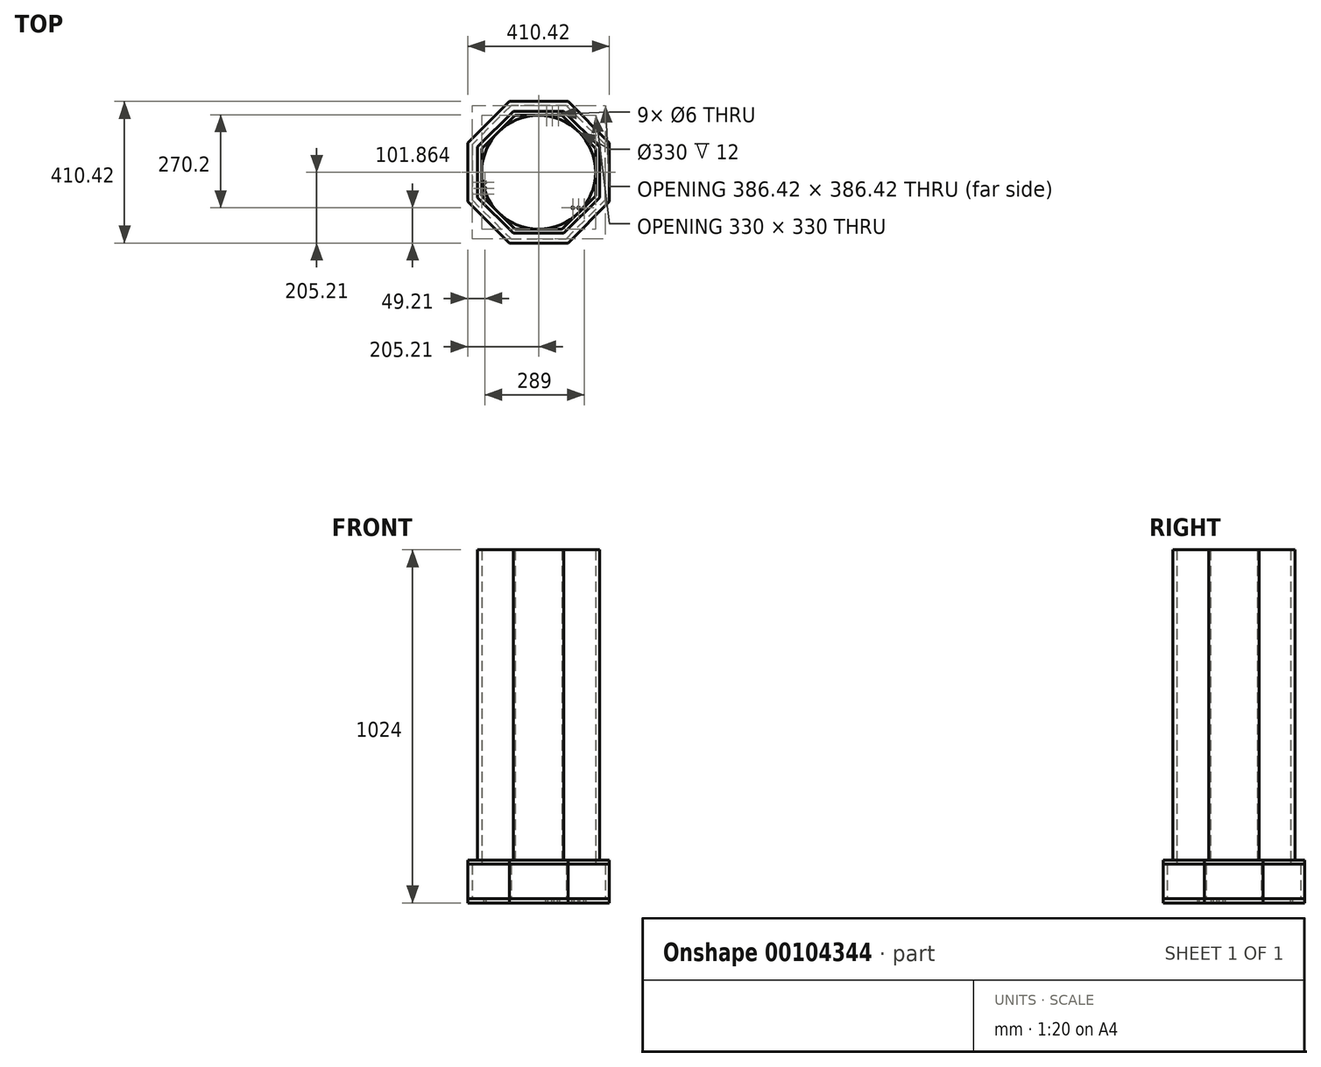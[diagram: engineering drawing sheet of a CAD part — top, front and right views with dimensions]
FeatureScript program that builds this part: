
annotation { "Feature Type Name" : "Feature", "Feature Type Description" : "" }
export const myFeature = defineFeature(function(context is Context, id is Id, definition is map)
    precondition{}
    {
        {
            var Q0;
            Q0=qCreatedBy(makeId("Top.planeOp"),FACE);
            var sketch = newSketch(context, id + "F0", { "sketchPlane" : qUnion([Q0])});
            skLineSegment(sketch, "E0.bottom", {"start": v(-85, 205.2) * mm, "end": v(85, 205.2) * mm});
            skLineSegment(sketch, "E0.top", {"start": v(-85, -205.2) * mm, "end": v(85, -205.2) * mm});
            skLineSegment(sketch, "E0.left", {"start": v(-205.2, 85) * mm, "end": v(-205.2, -85) * mm});
            skLineSegment(sketch, "E0.right", {"start": v(205.2, 85) * mm, "end": v(205.2, -85) * mm});
            skLineSegment(sketch, "E1", {"start": v(0, 127.02) * mm, "end": v(0, -63.5) * mm, "construction": true});
            skLineSegment(sketch, "E2", {"start": v(-110, -63.5) * mm, "end": v(55, 31.75) * mm, "construction": true});
            skLineSegment(sketch, "E3", {"start": v(110, -63.5) * mm, "end": v(-110, -63.5) * mm, "construction": true});
            skLineSegment(sketch, "E4", {"start": v(-110, -63.5) * mm, "end": v(-156, -63.5) * mm, "construction": true});
            skLineSegment(sketch, "E5", {"start": v(-110, -63.5) * mm, "end": v(0, 127.02) * mm, "construction": true});
            skLineSegment(sketch, "E6", {"start": v(0, 127.02) * mm, "end": v(110, -63.5) * mm, "construction": true});
            skLineSegment(sketch, "E7", {"start": v(-156, -63.5) * mm, "end": v(-156, -29.5) * mm, "construction": true});
            skCircle(sketch, "E8", {"center": v(-156, -29.5) * mm, "radius": 3 * mm});
            skCircle(sketch, "E9", {"center": v(-156, -46.5) * mm, "radius": 3 * mm});
            skCircle(sketch, "E10", {"center": v(-156, -63.5) * mm, "radius": 3 * mm});
            skPoint(sketch, "E11.center", {"position": v(0, 0) * mm});
            skLineSegment(sketch, "E12", {"start": v(0, 127.02) * mm, "end": v(23, 166.85) * mm, "construction": true});
            skLineSegment(sketch, "E13", {"start": v(110, -63.5) * mm, "end": v(133, -103.35) * mm, "construction": true});
            skLineSegment(sketch, "E14", {"start": v(23, 166.85) * mm, "end": v(57, 166.85) * mm, "construction": true});
            skLineSegment(sketch, "E15", {"start": v(99, -103.35) * mm, "end": v(133, -103.35) * mm, "construction": true});
            skCircle(sketch, "E16", {"center": v(23, 166.85) * mm, "radius": 3 * mm});
            skCircle(sketch, "E17", {"center": v(40, 166.85) * mm, "radius": 3 * mm});
            skCircle(sketch, "E18", {"center": v(57, 166.85) * mm, "radius": 3 * mm});
            skCircle(sketch, "E19", {"center": v(133, -103.35) * mm, "radius": 3 * mm});
            skCircle(sketch, "E20", {"center": v(116, -103.35) * mm, "radius": 3 * mm});
            skCircle(sketch, "E21", {"center": v(99, -103.35) * mm, "radius": 3 * mm});
            skLineSegment(sketch, "E22", {"start": v(-205.2, 85) * mm, "end": v(-85, 205.2) * mm});
            skCircle(sketch, "E23", {"center": v(0, 0) * mm, "radius": 205.2 * mm, "construction": true});
            skLineSegment(sketch, "E24", {"start": v(-205.2, -85) * mm, "end": v(-85, -205.2) * mm});
            skLineSegment(sketch, "E25", {"start": v(85, -205.2) * mm, "end": v(205.2, -85) * mm});
            skLineSegment(sketch, "E26", {"start": v(205.2, 85) * mm, "end": v(85, 205.2) * mm});
            skSolve(sketch);
        }
        {
            var Q0;
            Q0 = qSketchRegion(id + "F0", true);
            extrude(context, id + "F1", {"entities" : qUnion([Q0]), "depth" : 12 * mm});
        }
        {
            var Q0;
            Q0=makeQuery(id+"F1.opExtrude","CAP_FACE",FACE,{"disambiguationData":[OSD([sQuery(id+"F0.wireOp",EDGE,"E0.bottom"),sQuery(id+"F0.wireOp",EDGE,"E0.top"),sQuery(id+"F0.wireOp",EDGE,"E0.left"),sQuery(id+"F0.wireOp",EDGE,"E0.right"),sQuery(id+"F0.wireOp",EDGE,"E8"),sQuery(id+"F0.wireOp",EDGE,"E9"),sQuery(id+"F0.wireOp",EDGE,"E10"),sQuery(id+"F0.wireOp",EDGE,"E16"),sQuery(id+"F0.wireOp",EDGE,"E17"),sQuery(id+"F0.wireOp",EDGE,"E18"),sQuery(id+"F0.wireOp",EDGE,"E19"),sQuery(id+"F0.wireOp",EDGE,"E20"),sQuery(id+"F0.wireOp",EDGE,"E21"),sQuery(id+"F0.wireOp",EDGE,"E22"),sQuery(id+"F0.wireOp",EDGE,"E24"),sQuery(id+"F0.wireOp",EDGE,"E25"),sQuery(id+"F0.wireOp",EDGE,"E26")])],"isStart":false});
            var sketch = newSketch(context, id + "F2", { "sketchPlane" : qUnion([Q0])});
            skLineSegment(sketch, "E27", {"start": v(-80.03, -193.2) * mm, "end": v(80.03, -193.2) * mm});
            skLineSegment(sketch, "E28", {"start": v(80.03, -193.2) * mm, "end": v(193.2, -80.03) * mm});
            skLineSegment(sketch, "E29", {"start": v(193.2, -80.03) * mm, "end": v(193.2, 80.03) * mm});
            skLineSegment(sketch, "E30", {"start": v(193.2, 80.03) * mm, "end": v(80.03, 193.2) * mm});
            skLineSegment(sketch, "E31", {"start": v(80.03, 193.2) * mm, "end": v(-80.03, 193.2) * mm});
            skLineSegment(sketch, "E32", {"start": v(-80.03, 193.2) * mm, "end": v(-193.2, 80.03) * mm});
            skLineSegment(sketch, "E33", {"start": v(-193.2, 80.03) * mm, "end": v(-193.2, -80.03) * mm});
            skLineSegment(sketch, "E34", {"start": v(-193.2, -80.03) * mm, "end": v(-80.03, -193.2) * mm});
            skLineSegment(sketch, "E35", {"start": v(-205.2, 85) * mm, "end": v(-205.2, -85) * mm});
            skLineSegment(sketch, "E36", {"start": v(-205.2, -85) * mm, "end": v(-85, -205.2) * mm});
            skLineSegment(sketch, "E37", {"start": v(-85, -205.2) * mm, "end": v(85, -205.2) * mm});
            skLineSegment(sketch, "E38", {"start": v(85, -205.2) * mm, "end": v(205.2, -85) * mm});
            skLineSegment(sketch, "E39", {"start": v(205.2, -85) * mm, "end": v(205.2, 85) * mm});
            skLineSegment(sketch, "E40", {"start": v(205.2, 85) * mm, "end": v(85, 205.2) * mm});
            skLineSegment(sketch, "E41", {"start": v(85, 205.2) * mm, "end": v(-85, 205.2) * mm});
            skLineSegment(sketch, "E42", {"start": v(-85, 205.2) * mm, "end": v(-205.2, 85) * mm});
            skLineSegment(sketch, "E43", {"start": v(-193.2, 80.03) * mm, "end": v(-205.2, 80.03) * mm, "construction": true});
            skLineSegment(sketch, "E44", {"start": v(-80.03, 193.2) * mm, "end": v(-88.51, 201.7) * mm, "construction": true});
            skLineSegment(sketch, "E45", {"start": v(80.03, 193.2) * mm, "end": v(80.03, 205.2) * mm, "construction": true});
            skLineSegment(sketch, "E46", {"start": v(193.2, 80.03) * mm, "end": v(201.7, 88.51) * mm, "construction": true});
            skLineSegment(sketch, "E47", {"start": v(193.2, -80.03) * mm, "end": v(205.2, -80.03) * mm, "construction": true});
            skLineSegment(sketch, "E48", {"start": v(80.03, -193.2) * mm, "end": v(88.51, -201.7) * mm, "construction": true});
            skLineSegment(sketch, "E49", {"start": v(-80.03, -193.2) * mm, "end": v(-80.03, -205.2) * mm, "construction": true});
            skLineSegment(sketch, "E50", {"start": v(-193.2, -80.03) * mm, "end": v(-201.7, -88.51) * mm, "construction": true});
            skLineSegment(sketch, "E51", {"start": v(80.03, 193.2) * mm, "end": v(97, 193.2) * mm, "construction": true});
            skLineSegment(sketch, "E52", {"start": v(-80.03, 193.2) * mm, "end": v(-68.03, 205.2) * mm, "construction": true});
            skSolve(sketch);
        }
        {
            var Q0;
            Q0 = qSketchRegion(id + "F2", true);
            extrude(context, id + "F3", {"entities" : qUnion([Q0]), "depth" : 100 * mm});
        }
        {
            var Q0;
            Q0=makeQuery(id+"F3.opExtrude","CAP_FACE",FACE,{"disambiguationData":[OSD([sQuery(id+"F2.wireOp",EDGE,"E27"),sQuery(id+"F2.wireOp",EDGE,"E28"),sQuery(id+"F2.wireOp",EDGE,"E29"),sQuery(id+"F2.wireOp",EDGE,"E30"),sQuery(id+"F2.wireOp",EDGE,"E31"),sQuery(id+"F2.wireOp",EDGE,"E32"),sQuery(id+"F2.wireOp",EDGE,"E33"),sQuery(id+"F2.wireOp",EDGE,"E34"),sQuery(id+"F2.wireOp",EDGE,"E35"),sQuery(id+"F2.wireOp",EDGE,"E36"),sQuery(id+"F2.wireOp",EDGE,"E37"),sQuery(id+"F2.wireOp",EDGE,"E38"),sQuery(id+"F2.wireOp",EDGE,"E39"),sQuery(id+"F2.wireOp",EDGE,"E40"),sQuery(id+"F2.wireOp",EDGE,"E41"),sQuery(id+"F2.wireOp",EDGE,"E42")])],"isStart":false});
            var sketch = newSketch(context, id + "F4", { "sketchPlane" : qUnion([Q0])});
            skPoint(sketch, "E53.middle", {"position": v(0, 0) * mm});
            skCircle(sketch, "E54", {"center": v(0, 0) * mm, "radius": 165 * mm});
            skLineSegment(sketch, "E55.bottom", {"start": v(85, 205.2) * mm, "end": v(-85, 205.2) * mm});
            skLineSegment(sketch, "E55.top", {"start": v(85, -205.2) * mm, "end": v(-85, -205.2) * mm});
            skLineSegment(sketch, "E55.left", {"start": v(205.2, 85) * mm, "end": v(205.2, -85) * mm});
            skLineSegment(sketch, "E55.right", {"start": v(-205.2, 85) * mm, "end": v(-205.2, -85) * mm});
            skLineSegment(sketch, "E56", {"start": v(-85, 205.2) * mm, "end": v(-205.2, 85) * mm});
            skLineSegment(sketch, "E57", {"start": v(-205.2, -85) * mm, "end": v(-85, -205.2) * mm});
            skLineSegment(sketch, "E58", {"start": v(85, -205.2) * mm, "end": v(205.2, -85) * mm});
            skLineSegment(sketch, "E59", {"start": v(205.2, 85) * mm, "end": v(85, 205.2) * mm});
            skSolve(sketch);
        }
        {
            var Q0;
            Q0 = qSketchRegion(id + "F4", true);
            extrude(context, id + "F5", {"entities" : qUnion([Q0]), "depth" : 12 * mm});
        }
        {
            var Q0;
            Q0=makeQuery(id+"F5.opExtrude","CAP_FACE",FACE,{"disambiguationData":[OSD([sQuery(id+"F4.wireOp",EDGE,"E54"),sQuery(id+"F4.wireOp",EDGE,"E55.bottom"),sQuery(id+"F4.wireOp",EDGE,"E55.top"),sQuery(id+"F4.wireOp",EDGE,"E55.left"),sQuery(id+"F4.wireOp",EDGE,"E55.right")])],"isStart":false});
            var sketch = newSketch(context, id + "F6", { "sketchPlane" : qUnion([Q0])});
            skLineSegment(sketch, "E60", {"start": v(-68.35, 165) * mm, "end": v(-56.35, 177) * mm});
            skLineSegment(sketch, "E61", {"start": v(-56.35, 177) * mm, "end": v(73.32, 177) * mm});
            skLineSegment(sketch, "E62", {"start": v(73.32, 177) * mm, "end": v(177, 73.32) * mm});
            skLineSegment(sketch, "E63", {"start": v(68.35, 165) * mm, "end": v(-68.35, 165) * mm});
            skLineSegment(sketch, "E64", {"start": v(-56.35, 177) * mm, "end": v(-165, 68.35) * mm});
            skLineSegment(sketch, "E65", {"start": v(-165, 68.35) * mm, "end": v(-165, 85.32) * mm});
            skLineSegment(sketch, "E66", {"start": v(-165, 85.32) * mm, "end": v(-73.32, 177) * mm});
            skLineSegment(sketch, "E67", {"start": v(-73.32, 177) * mm, "end": v(-56.35, 177) * mm});
            skLineSegment(sketch, "E68", {"start": v(-165, 85.32) * mm, "end": v(-177, 73.32) * mm});
            skLineSegment(sketch, "E69", {"start": v(-177, 73.32) * mm, "end": v(-177, -73.32) * mm});
            skLineSegment(sketch, "E70", {"start": v(-177, -73.32) * mm, "end": v(-73.32, -177) * mm});
            skLineSegment(sketch, "E71", {"start": v(-165, -68.35) * mm, "end": v(-165, 85.32) * mm});
            skLineSegment(sketch, "E72", {"start": v(-165, -68.35) * mm, "end": v(-68.35, -165) * mm});
            skLineSegment(sketch, "E73", {"start": v(-68.35, -165) * mm, "end": v(68.35, -165) * mm});
            skLineSegment(sketch, "E74", {"start": v(68.35, -165) * mm, "end": v(165, -68.35) * mm});
            skLineSegment(sketch, "E75", {"start": v(165, -68.35) * mm, "end": v(165, 68.35) * mm});
            skLineSegment(sketch, "E76", {"start": v(165, 68.35) * mm, "end": v(68.35, 165) * mm});
            skLineSegment(sketch, "E77", {"start": v(-73.32, -177) * mm, "end": v(73.32, -177) * mm});
            skLineSegment(sketch, "E78", {"start": v(73.32, -177) * mm, "end": v(177, -73.32) * mm});
            skLineSegment(sketch, "E79", {"start": v(177, -73.32) * mm, "end": v(177, 73.32) * mm});
            skLineSegment(sketch, "E80", {"start": v(165, 68.35) * mm, "end": v(177, 68.35) * mm, "construction": true});
            skLineSegment(sketch, "E81", {"start": v(-68.35, -165) * mm, "end": v(-68.35, -177) * mm, "construction": true});
            skLineSegment(sketch, "E82", {"start": v(68.35, 165) * mm, "end": v(76.83, 173.49) * mm, "construction": true});
            skLineSegment(sketch, "E83", {"start": v(-165, -68.35) * mm, "end": v(-173.49, -76.83) * mm, "construction": true});
            skLineSegment(sketch, "E84", {"start": v(165, -68.35) * mm, "end": v(173.49, -76.83) * mm, "construction": true});
            skLineSegment(sketch, "E85", {"start": v(68.35, 165) * mm, "end": v(68.35, 177) * mm, "construction": true});
            skSolve(sketch);
        }
        {
            var Q0;
            Q0 = qSketchRegion(id + "F6", true);
            extrude(context, id + "F7", {"entities" : qUnion([Q0]), "depth" : 900 * mm});
        }
    });
